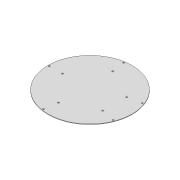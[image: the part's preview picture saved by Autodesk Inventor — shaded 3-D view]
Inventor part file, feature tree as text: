
AUTODESK INVENTOR PART (.ipt)
format: ipt  version: 2021 (Build 250183000, 183)  size: 106,496 bytes
history: native  units: mm
features: extrude x1, sketch x1
ambient origin geometry x8: Origin, YZ Plane, XZ Plane, XY Plane, X Axis, Y Axis, Z Axis, Center Point
bodies: Solid1 (feature_tree)
feature tree (2):
  extrude  "Extrusion1"  Depth=7.0mm
  sketch  "Sketch1"  dims[d0=504.787567mm d1=944.787567mm d34=1152.87mm d52=20.0mm d55=20.0mm d58=556.435mm d59=20.0mm d60=376.435mm d61=20.0mm d62=556.435mm d63=20.0mm d65=14.137167mm d67=20.0mm d69=14.137167mm d71=7.0mm d72=0.0mm]
